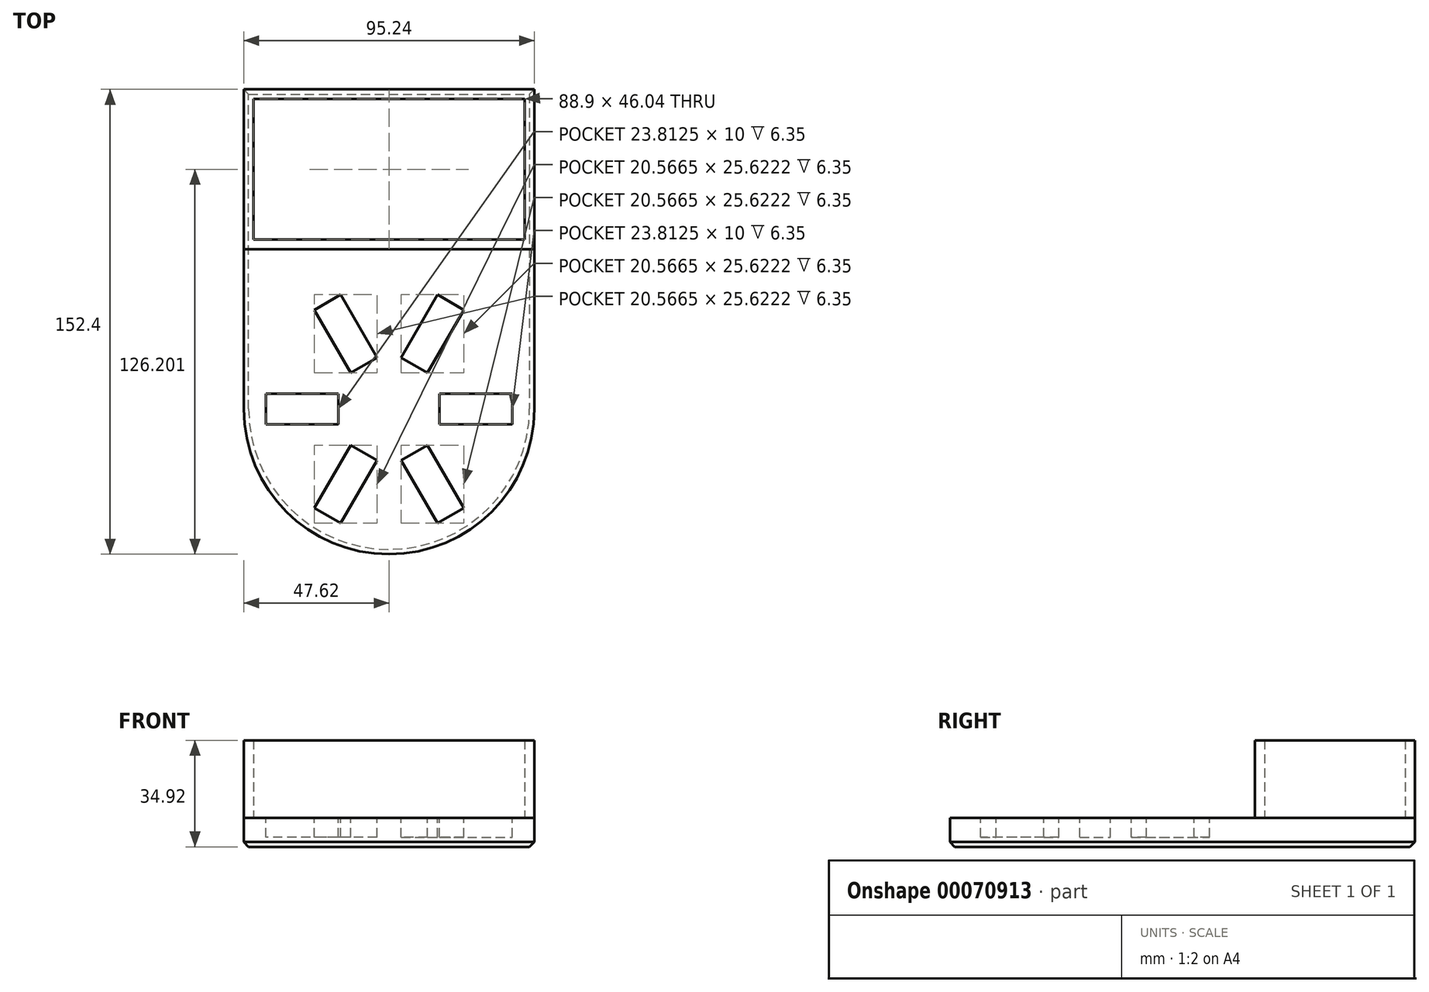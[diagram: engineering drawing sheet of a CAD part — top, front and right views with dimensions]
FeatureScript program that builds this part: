
annotation { "Feature Type Name" : "Feature", "Feature Type Description" : "" }
export const myFeature = defineFeature(function(context is Context, id is Id, definition is map)
    precondition{}
    {
        {
            var Q0;
            Q0=qCreatedBy(makeId("Top.planeOp"),FACE);
            var sketch = newSketch(context, id + "F0", { "sketchPlane" : qUnion([Q0])});
            skCircle(sketch, "E0", {"center": v(0, 0) * mm, "radius": 47.63 * mm});
            skCircle(sketch, "E1", {"center": v(0, 0) * mm, "radius": 12.7 * mm});
            skLineSegment(sketch, "E2.top", {"start": v(-47.63, 104.78) * mm, "end": v(47.63, 104.78) * mm});
            skLineSegment(sketch, "E2.left", {"start": v(-47.63, 0) * mm, "end": v(-47.63, 104.78) * mm});
            skLineSegment(sketch, "E2.right", {"start": v(47.63, 0) * mm, "end": v(47.63, 104.78) * mm});
            skLineSegment(sketch, "E3.bottom", {"start": v(-44.45, 101.6) * mm, "end": v(44.45, 101.6) * mm});
            skLineSegment(sketch, "E3.top", {"start": v(-44.45, 55.56) * mm, "end": v(44.45, 55.56) * mm});
            skLineSegment(sketch, "E3.left", {"start": v(-44.45, 101.6) * mm, "end": v(-44.45, 55.56) * mm});
            skLineSegment(sketch, "E3.right", {"start": v(44.45, 101.6) * mm, "end": v(44.45, 55.56) * mm});
            skLineSegment(sketch, "E4", {"start": v(-47.63, 52.39) * mm, "end": v(47.63, 52.39) * mm});
            skSolve(sketch);
        }
        {
            var Q0;
            Q0=makeQuery(id+"F0.imprint","IMPRINT",FACE,{"disambiguationData":[TD([[makeQuery(id+"F0.imprint","IMPRINT",EDGE,{"derivedFrom":sQuery(id+"F0.wireOp",EDGE,"E0")}),1.0]])]});
            var Q1;
            {var subQ5=sQuery(id+"F0.wireOp",EDGE,"E4");Q1=makeQuery(id+"F0.imprint","IMPRINT",FACE,{"disambiguationData":[TD([[makeQuery(id+"F0.imprint","IMPRINT",EDGE,{"derivedFrom":subQ5}),-1.0]])]});}
            var Q2;
            Q2=makeQuery(id+"F0.imprint","IMPRINT",FACE,{"disambiguationData":[TD([[makeQuery(id+"F0.imprint","IMPRINT",EDGE,{"derivedFrom":sQuery(id+"F0.wireOp",EDGE,"E3.bottom")}),-1.0]])]});
            var Q3;
            {var subQ1=sQuery(id+"F0.wireOp",EDGE,"E2.top");Q3=makeQuery(id+"F0.imprint","IMPRINT",FACE,{"disambiguationData":[TD([[makeQuery(id+"F0.imprint","IMPRINT",EDGE,{"derivedFrom":subQ1}),-1.0]])]});}
            extrude(context, id + "F1", {"entities" : qUnion([Q0, Q1, Q2, Q3]), "depth" : 9.52 * mm});
        }
        {
            var Q0;
            Q0=makeQuery(id+"F1.opExtrude","CAP_FACE",FACE,{"disambiguationData":[OSD([sQuery(id+"F0.wireOp",EDGE,"E0"),sQuery(id+"F0.wireOp",EDGE,"E1"),sQuery(id+"F0.wireOp",EDGE,"E2.top"),sQuery(id+"F0.wireOp",EDGE,"E2.left"),sQuery(id+"F0.wireOp",EDGE,"E2.right")])],"isStart":false});
            var sketch = newSketch(context, id + "F2", { "sketchPlane" : qUnion([Q0])});
            skLineSegment(sketch, "E5.0", {"start": v(-44.45, 101.6) * mm, "end": v(44.45, 101.6) * mm});
            skLineSegment(sketch, "E6.0", {"start": v(-44.45, 101.6) * mm, "end": v(-44.45, 55.56) * mm});
            skLineSegment(sketch, "E7.0", {"start": v(-44.45, 55.56) * mm, "end": v(44.45, 55.56) * mm});
            skLineSegment(sketch, "E8.0", {"start": v(44.45, 101.6) * mm, "end": v(44.45, 55.56) * mm});
            skLineSegment(sketch, "E9.0", {"start": v(-47.63, 52.39) * mm, "end": v(47.63, 52.39) * mm});
            skPoint(sketch, "E10.0", {"position": v(-47.63, 104.78) * mm});
            skPoint(sketch, "E11.0", {"position": v(47.63, 104.78) * mm});
            skLineSegment(sketch, "E12.top", {"start": v(-47.63, 104.78) * mm, "end": v(47.63, 104.78) * mm});
            skLineSegment(sketch, "E12.left", {"start": v(-47.63, 52.39) * mm, "end": v(-47.63, 104.78) * mm});
            skLineSegment(sketch, "E12.right", {"start": v(47.63, 52.39) * mm, "end": v(47.63, 104.78) * mm});
            skLineSegment(sketch, "E13.bottom", {"start": v(44.45, 55.56) * mm, "end": v(-44.45, 55.56) * mm});
            skLineSegment(sketch, "E13.top", {"start": v(44.45, 101.6) * mm, "end": v(-44.45, 101.6) * mm});
            skLineSegment(sketch, "E13.left", {"start": v(44.45, 55.56) * mm, "end": v(44.45, 101.6) * mm});
            skLineSegment(sketch, "E13.right", {"start": v(-44.45, 55.56) * mm, "end": v(-44.45, 101.6) * mm});
            skSolve(sketch);
        }
        {
            var Q0;
            Q0=makeQuery(id+"F2.imprint","IMPRINT",FACE,{"disambiguationData":[TD([[makeQuery(id+"F2.imprint","IMPRINT",EDGE,{"derivedFrom":sQuery(id+"F2.wireOp",EDGE,"E9.0")}),1.0]])]});
            extrude(context, id + "F3", {"entities" : qUnion([Q0]), "depth" : 25.4 * mm});
        }
        {
            var Q0;
            Q0=makeQuery(id+"F1.opExtrude","CAP_FACE",FACE,{"disambiguationData":[OSD([sQuery(id+"F0.wireOp",EDGE,"E0"),sQuery(id+"F0.wireOp",EDGE,"E1")])],"isStart":false});
            var sketch = newSketch(context, id + "F4", { "sketchPlane" : qUnion([Q0])});
            skLineSegment(sketch, "E14.rect.bottom", {"start": v(-16.57, -5) * mm, "end": v(-40.39, -5) * mm});
            skLineSegment(sketch, "E14.rect.top", {"start": v(-16.57, 5) * mm, "end": v(-40.39, 5) * mm});
            skLineSegment(sketch, "E14.rect.left", {"start": v(-16.57, -5) * mm, "end": v(-16.57, 5) * mm});
            skLineSegment(sketch, "E14.rect.right", {"start": v(-40.39, -5) * mm, "end": v(-40.39, 5) * mm});
            skPoint(sketch, "E14.rect.middle", {"position": v(-28.48, 0) * mm});
            skLineSegment(sketch, "E15", {"start": v(-47.63, 0) * mm, "end": v(-12.7, 0) * mm, "construction": true});
            skPoint(sketch, "E15.startSnap0", {"position": v(-40.39, 0) * mm});
            skPoint(sketch, "E15.endSnap0", {"position": v(-16.57, 0) * mm});
            skLineSegment(sketch, "E16.1.0", {"start": v(-12.62, -11.85) * mm, "end": v(-24.52, -32.48) * mm});
            skLineSegment(sketch, "E16.1.1", {"start": v(-3.96, -16.85) * mm, "end": v(-15.86, -37.48) * mm});
            skLineSegment(sketch, "E16.1.2", {"start": v(-3.96, -16.85) * mm, "end": v(-12.62, -11.85) * mm});
            skLineSegment(sketch, "E16.1.3", {"start": v(-15.86, -37.48) * mm, "end": v(-24.52, -32.48) * mm});
            skLineSegment(sketch, "E16.2.0", {"start": v(3.96, -16.85) * mm, "end": v(15.86, -37.48) * mm});
            skLineSegment(sketch, "E16.2.1", {"start": v(12.62, -11.85) * mm, "end": v(24.52, -32.48) * mm});
            skLineSegment(sketch, "E16.2.2", {"start": v(12.62, -11.85) * mm, "end": v(3.96, -16.85) * mm});
            skLineSegment(sketch, "E16.2.3", {"start": v(24.52, -32.48) * mm, "end": v(15.86, -37.48) * mm});
            skLineSegment(sketch, "E16.3.0", {"start": v(16.57, -5) * mm, "end": v(40.39, -5) * mm});
            skLineSegment(sketch, "E16.3.1", {"start": v(16.57, 5) * mm, "end": v(40.39, 5) * mm});
            skLineSegment(sketch, "E16.3.2", {"start": v(16.57, 5) * mm, "end": v(16.57, -5) * mm});
            skLineSegment(sketch, "E16.3.3", {"start": v(40.39, 5) * mm, "end": v(40.39, -5) * mm});
            skLineSegment(sketch, "E16.4.0", {"start": v(12.62, 11.85) * mm, "end": v(24.52, 32.48) * mm});
            skLineSegment(sketch, "E16.4.1", {"start": v(3.96, 16.85) * mm, "end": v(15.86, 37.48) * mm});
            skLineSegment(sketch, "E16.4.2", {"start": v(3.96, 16.85) * mm, "end": v(12.62, 11.85) * mm});
            skLineSegment(sketch, "E16.4.3", {"start": v(15.86, 37.48) * mm, "end": v(24.52, 32.48) * mm});
            skLineSegment(sketch, "E16.5.0", {"start": v(-3.96, 16.85) * mm, "end": v(-15.86, 37.48) * mm});
            skLineSegment(sketch, "E16.5.1", {"start": v(-12.62, 11.85) * mm, "end": v(-24.52, 32.48) * mm});
            skLineSegment(sketch, "E16.5.2", {"start": v(-12.62, 11.85) * mm, "end": v(-3.96, 16.85) * mm});
            skLineSegment(sketch, "E16.5.3", {"start": v(-24.52, 32.48) * mm, "end": v(-15.86, 37.48) * mm});
            skPoint(sketch, "E16.center", {"position": v(0, 0) * mm});
            skSolve(sketch);
        }
        {
            var Q0;
            Q0=makeQuery(id+"F4.imprint","IMPRINT",FACE,{"disambiguationData":[TD([[makeQuery(id+"F4.imprint","IMPRINT",EDGE,{"derivedFrom":sQuery(id+"F4.wireOp",EDGE,"E14.rect.bottom")}),-1.0]])]});
            var Q1;
            Q1=makeQuery(id+"F4.imprint","IMPRINT",FACE,{"disambiguationData":[TD([[makeQuery(id+"F4.imprint","IMPRINT",EDGE,{"derivedFrom":sQuery(id+"F4.wireOp",EDGE,"E16.5.0")}),1.0]])]});
            var Q2;
            Q2=makeQuery(id+"F4.imprint","IMPRINT",FACE,{"disambiguationData":[TD([[makeQuery(id+"F4.imprint","IMPRINT",EDGE,{"derivedFrom":sQuery(id+"F4.wireOp",EDGE,"E16.4.0")}),1.0]])]});
            var Q3;
            Q3=makeQuery(id+"F4.imprint","IMPRINT",FACE,{"disambiguationData":[TD([[makeQuery(id+"F4.imprint","IMPRINT",EDGE,{"derivedFrom":sQuery(id+"F4.wireOp",EDGE,"E16.3.0")}),1.0]])]});
            var Q4;
            Q4=makeQuery(id+"F4.imprint","IMPRINT",FACE,{"disambiguationData":[TD([[makeQuery(id+"F4.imprint","IMPRINT",EDGE,{"derivedFrom":sQuery(id+"F4.wireOp",EDGE,"E16.2.0")}),1.0]])]});
            var Q5;
            Q5=makeQuery(id+"F4.imprint","IMPRINT",FACE,{"disambiguationData":[TD([[makeQuery(id+"F4.imprint","IMPRINT",EDGE,{"derivedFrom":sQuery(id+"F4.wireOp",EDGE,"E16.1.0")}),1.0]])]});
            extrude(context, id + "F5", {"entities" : qUnion([Q0, Q1, Q2, Q3, Q4, Q5]), "operationType" : NewBodyOperationType.REMOVE, "oppositeDirection" : true, "depth" : 6.35 * mm});
        }
        {
            var Q0;
            Q0=makeQuery(id+"F0.imprint","IMPRINT",FACE,{"disambiguationData":[TD([[makeQuery(id+"F0.imprint","IMPRINT",EDGE,{"derivedFrom":sQuery(id+"F0.wireOp",EDGE,"E1")}),1.0]])]});
            var Q1;
            Q1=makeQuery(id+"F1.opExtrude","CAP_FACE",FACE,{"disambiguationData":[OSD([sQuery(id+"F0.wireOp",EDGE,"E0"),sQuery(id+"F0.wireOp",EDGE,"E1")])],"isStart":false});
            extrude(context, id + "F6", {"entities" : qUnion([Q0]), "operationType" : NewBodyOperationType.ADD, "endBound" : BoundingType.UP_TO_SURFACE, "endBoundEntityFace" : qUnion([Q1]), "depth" : 25.4 * mm});
        }
        {
            var Q0;
            Q0=makeQuery(id+"F1.opExtrude","CAP_EDGE",EDGE,{"disambiguationData":[OSD([sQuery(id+"F0.wireOp",EDGE,"E0")])],"isStart":true});
            var Q1;
            Q1=makeQuery(id+"F1.opExtrude","CAP_EDGE",EDGE,{"disambiguationData":[OSD([sQuery(id+"F0.wireOp",EDGE,"E2.top")])],"isStart":true});
            chamfer(context, id + "F7", {"entities" : qUnion([Q0, Q1]), "width" : 1.59 * mm, "tangentPropagation" : true});
        }
    });
